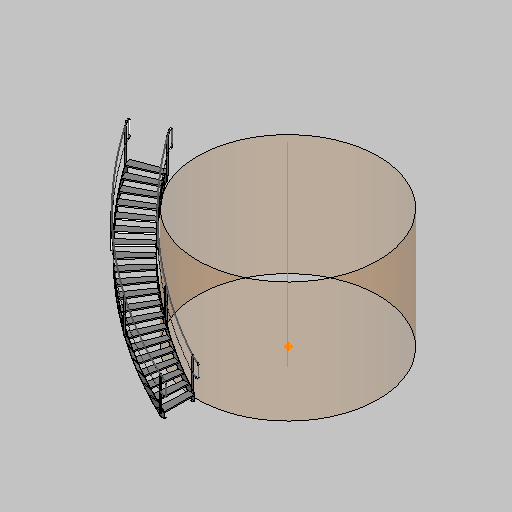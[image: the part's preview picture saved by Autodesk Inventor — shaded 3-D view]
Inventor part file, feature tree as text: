
AUTODESK INVENTOR PART (.ipt)
format: ipt  version: 2025.2 (Build 292293000, 293)  size: 775,168 bytes
history: native  units: mm
features: projected_geometry x6, other x4, extrude x4, sketch x4, plane x3, pattern_linear x2, helix x2, sweep x2, revolve x1, split x1
ambient origin geometry x7: Origin, YZ Plane, XZ Plane, X Axis, Y Axis, Z Axis, Center Point
bodies: Solid1 (feature_tree)
feature tree (29):
  other  "First Step"
  extrude  "Extrusion1"  Depth=40.0mm TaperAngle=0.0deg
  sketch  "3D Sketch3"
  pattern_linear  "Rectangular Pattern1"  Count1=600 Spacing1=1.835662mm
  helix  "Coil1"  [1 undecoded]
  revolve  "Revolution1"  [1 undecoded]
  split  "Split1"
  plane  "Work Plane2"
  extrude  "Extrusion5"  Depth=10.0mm
  helix  "Coil2"  [1 undecoded]
  pattern_linear  "Rectangular Pattern3"  Count1=5  [1 undecoded]
  extrude  "Extrusion6"  TaperAngle=60.0deg  [1 undecoded]
  plane  "Work Plane3"
  sweep  "Sweep1"
  sketch  "Sketch14"  dims[d24=300.0mm d25=10.0mm d26=21790.499968mm d27=10.0mm d28=1.835662mm d29=0.0mm d30=90.0deg d31=90.0deg d32=0.0mm d33=0.0mm d38=0.383972mm d49=50.0mm d51=60.0deg d52=10.0mm d53=0.0mm d54=-100.0mm d55=1050.0mm d57=48.0mm d58=21.0mm d59=21.0mm d60=500.0mm d61=21790.499968mm d62=10.0mm d63=1.835662mm d64=0.0mm d65=90.0deg d66=90.0deg d67=0.0mm d68=0.0mm d72=50.0mm d73=50.0mm d74=10.0mm d75=0.0mm d76=250.0mm d77=6.981317mm d78=50.0mm d79=0.0mm d80=0.0mm d81=0.0mm d82=100.0mm d83=8.726646mm d84=200.0mm d85=75.0mm d86=0.0mm d87=0.0mm d88=6000.0mm d89=4000.0mm d90=0.0mm]
  plane  "Work Plane4"
  sweep  "Sweep2"
  other  "Ground Plane"
  other  "Helical Curve2"
  sketch  "Sketch8"  dims[d6=260.0mm d7=40.0mm d8=0.0mm]
  projected_geometry  "Projected Loop1"
  sketch  "Sketch9"  dims[d13=21790.499968mm d14=1.835662mm d15=6000.0mm d16=0.0mm d21=200.0mm]
  projected_geometry  "Projected Loop2"
  projected_geometry  "Projected Loop3"
  projected_geometry  "Projected Loop4"
  projected_geometry  "Projected Loop5"
  projected_geometry  "Projected Loop6"
  other  "Srf1"
  extrude  "ExtrusionSrf1"  Depth=10.0mm
note: 5 required parameter values undecoded (feature->parameter linkage not recoverable at this tier; creation-order binding heuristic only, values carry confidence <= 0.55)